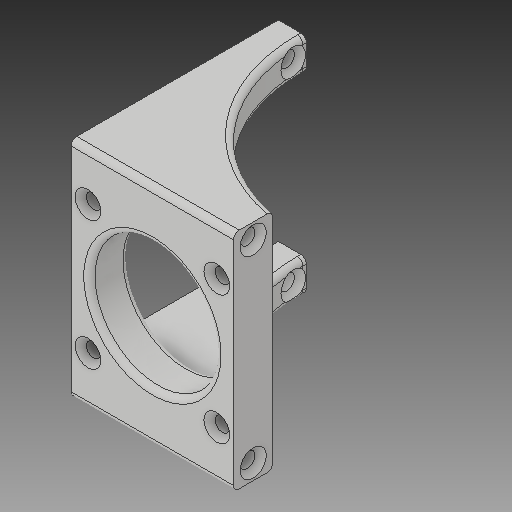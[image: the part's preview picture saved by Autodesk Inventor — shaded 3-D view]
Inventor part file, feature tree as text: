
AUTODESK INVENTOR PART (.ipt)
format: ipt  version: 2019 (Build 230136000, 136)  size: 314,880 bytes
history: native  units: mm
features: fillet x4, extrude x3, sketch x3, chamfer x2
ambient origin geometry x8: Origin, YZ Plane, XZ Plane, XY Plane, X Axis, Y Axis, Z Axis, Center Point
bodies: Solid1 (feature_tree)
feature tree (12):
  extrude  "Extrusion1"  Depth=23.0mm
  extrude  "Extrusion2"  Depth=40.0mm
  fillet  "Fillet1"  Radius=22.5mm
  extrude  "Extrusion3"  Depth=1.0mm
  chamfer  "Chamfer1"  Distance=2.6mm
  chamfer  "Chamfer2"  Distance=2.6mm
  fillet  "Fillet2"  Radius=7.0mm
  fillet  "Fillet3"  Radius=5.0mm
  fillet  "Fillet4"  Radius=40.0mm
  sketch  "Sketch1"  dims[d0=23.0mm d1=23.0mm]
  sketch  "Sketch2"  dims[d2=29.0mm d3=40.0mm d4=22.5mm]
  sketch  "Sketch3"  dims[d5=2.6mm d6=2.6mm d7=2.6mm d8=2.6mm d9=7.0mm d10=0.0mm d11=5.0mm d12=40.0mm d13=28.5mm d14=28.5mm d15=30.0mm d16=0.0mm d17=30.0mm d18=12.0mm d19=31.0mm d20=34.5mm d21=2.7mm d22=2.7mm d23=2.7mm d24=2.7mm d25=30.0mm d26=0.0mm d27=1.0mm d28=2.0mm d29=45.0deg d30=1.0mm d31=2.0mm d32=45.0deg d33=1.0mm d34=1.0mm d35=1.0mm]
